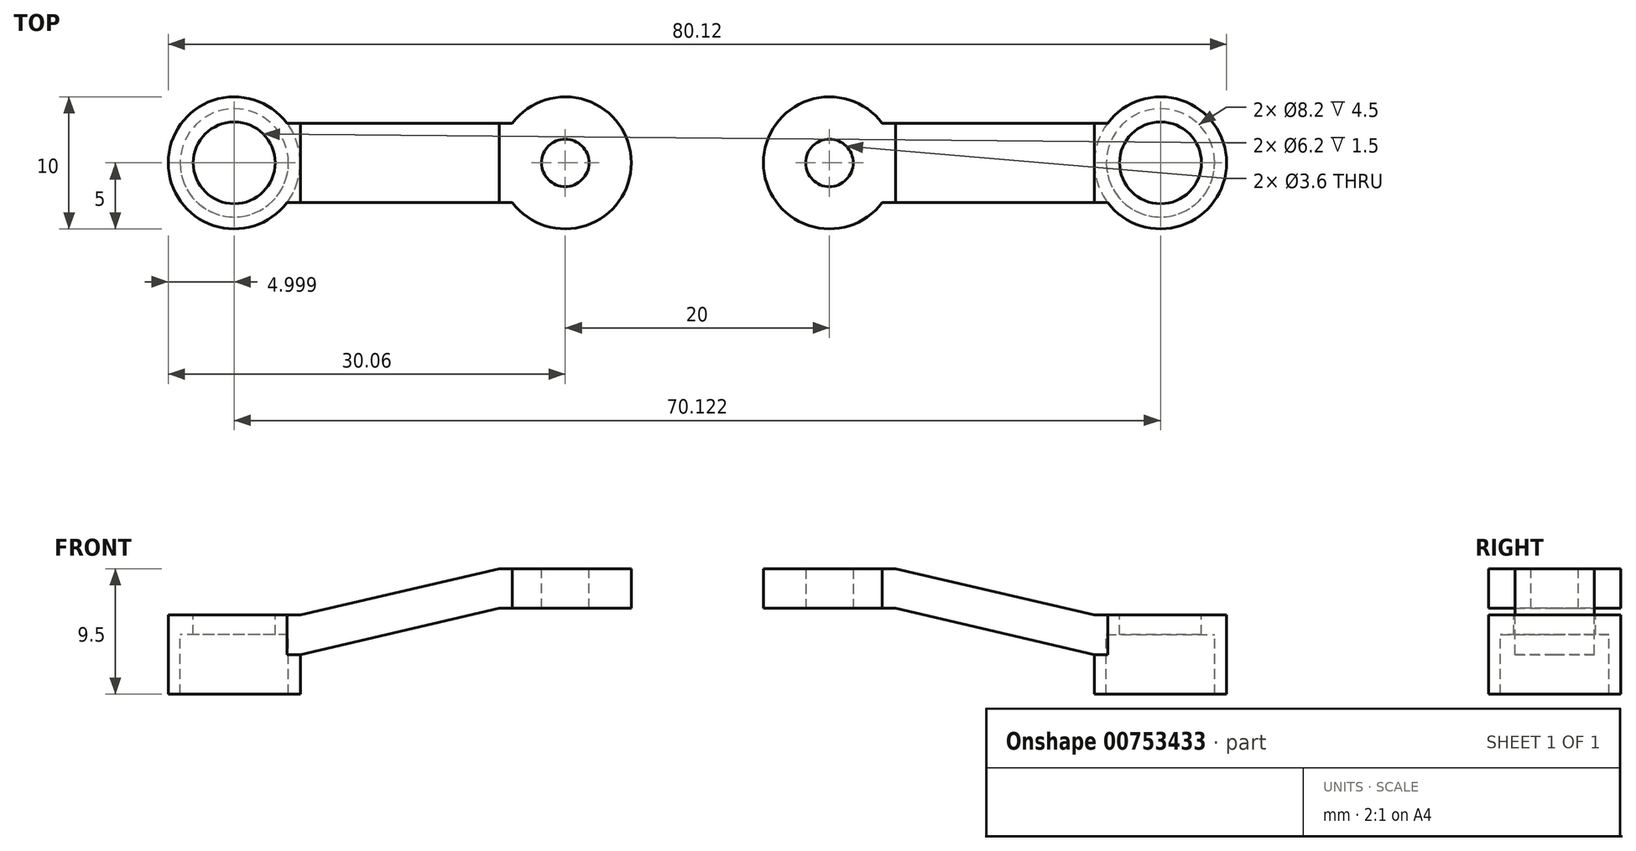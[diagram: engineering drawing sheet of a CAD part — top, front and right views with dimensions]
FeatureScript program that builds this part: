
annotation { "Feature Type Name" : "Feature", "Feature Type Description" : "" }
export const myFeature = defineFeature(function(context is Context, id is Id, definition is map)
    precondition{}
    {
        {
            var Q0;
            Q0=qCreatedBy(makeId("Front.planeOp"),FACE);
            var sketch = newSketch(context, id + "F0", { "sketchPlane" : qUnion([Q0])});
            skLineSegment(sketch, "E0", {"start": v(-30.06, 0) * mm, "end": v(-20.06, 0) * mm});
            skLineSegment(sketch, "E1", {"start": v(5, 3.5) * mm, "end": v(5, 6.5) * mm});
            skLineSegment(sketch, "E2", {"start": v(-20.06, 3) * mm, "end": v(-30.06, 3) * mm});
            skLineSegment(sketch, "E3", {"start": v(-30.06, 3) * mm, "end": v(-30.06, 0) * mm});
            skLineSegment(sketch, "E4", {"start": v(-5, 3.5) * mm, "end": v(-5, 6.5) * mm});
            skLineSegment(sketch, "E5", {"start": v(-20.06, 0) * mm, "end": v(-20.06, 3) * mm});
            skLineSegment(sketch, "E6", {"start": v(5, 6.5) * mm, "end": v(-5, 6.5) * mm});
            skLineSegment(sketch, "E7", {"start": v(5, 3.5) * mm, "end": v(-5, 3.5) * mm});
            skLineSegment(sketch, "E8", {"start": v(-20.06, 0) * mm, "end": v(-5, 3.5) * mm});
            skLineSegment(sketch, "E9", {"start": v(-5, 6.5) * mm, "end": v(-20.06, 3) * mm});
            skLineSegment(sketch, "E10", {"start": v(-25.06, 3) * mm, "end": v(-25.06, 0) * mm, "construction": true});
            skLineSegment(sketch, "E11", {"start": v(0, 6.5) * mm, "end": v(0, 3.5) * mm, "construction": true});
            skSolve(sketch);
        }
        {
            var Q0;
            Q0=makeQuery(id+"F0.imprint","IMPRINT",FACE,{"disambiguationData":[TD([[makeQuery(id+"F0.imprint","IMPRINT",EDGE,{"derivedFrom":sQuery(id+"F0.wireOp",EDGE,"E0")}),1.0]])]});
            var Q1;
            Q1=makeQuery(id+"F0.imprint","IMPRINT",FACE,{"disambiguationData":[TD([[makeQuery(id+"F0.imprint","IMPRINT",EDGE,{"derivedFrom":sQuery(id+"F0.wireOp",EDGE,"E4")}),1.0]])]});
            var Q2;
            Q2=makeQuery(id+"F0.imprint","IMPRINT",FACE,{"disambiguationData":[TD([[makeQuery(id+"F0.imprint","IMPRINT",EDGE,{"derivedFrom":sQuery(id+"F0.wireOp",EDGE,"E1")}),1.0]])]});
            extrude(context, id + "F1", {"entities" : qUnion([Q0, Q1, Q2]), "depth" : 7 * mm, "offsetDistance" : 25 * mm, "hasSecondDirection" : true, "secondDirectionOppositeDirection" : true, "secondDirectionDepth" : 7 * mm});
        }
        {
            var Q0;
            Q0=makeQuery(id+"F1.opExtrude","SWEPT_FACE",FACE,{"disambiguationData":[OSD([sQuery(id+"F0.wireOp",EDGE,"E6")])]});
            var sketch = newSketch(context, id + "F2", { "sketchPlane" : qUnion([Q0])});
            skCircle(sketch, "E12", {"center": v(0, 0) * mm, "radius": 4.1 * mm, "construction": true});
            skLineSegment(sketch, "E13.0", {"start": v(-20.06, 7) * mm, "end": v(-30.06, 7) * mm});
            skLineSegment(sketch, "E14.0", {"start": v(-30.06, -7) * mm, "end": v(-30.06, 7) * mm});
            skCircle(sketch, "E15", {"center": v(-25.06, 0) * mm, "radius": 4.1 * mm});
            skPoint(sketch, "E15.centerSnap0", {"position": v(-25.06, 7) * mm});
            skLineSegment(sketch, "E16.0", {"start": v(-5, 7) * mm, "end": v(-20.06, 7) * mm});
            skLineSegment(sketch, "E17.0", {"start": v(-20.06, -7) * mm, "end": v(-30.06, -7) * mm});
            skLineSegment(sketch, "E18.0", {"start": v(-5, -7) * mm, "end": v(-20.06, -7) * mm});
            skLineSegment(sketch, "E19.0", {"start": v(5, -7) * mm, "end": v(-5, -7) * mm});
            skLineSegment(sketch, "E20.0", {"start": v(5, -7) * mm, "end": v(5, 7) * mm});
            skLineSegment(sketch, "E21.0", {"start": v(5, 7) * mm, "end": v(-5, 7) * mm});
            skLineSegment(sketch, "E22", {"start": v(-21.06, 3) * mm, "end": v(-4, 3) * mm});
            skLineSegment(sketch, "E23", {"start": v(-21.06, -3) * mm, "end": v(-4, -3) * mm});
            skLineSegment(sketch, "E24", {"start": v(-25.06, 0) * mm, "end": v(0, 0) * mm, "construction": true});
            skLineSegment(sketch, "E25", {"start": v(-4, 3) * mm, "end": v(0, 3) * mm});
            skLineSegment(sketch, "E26", {"start": v(-4, -3) * mm, "end": v(0, -3) * mm});
            skCircle(sketch, "E27", {"center": v(-25.06, 0) * mm, "radius": 5 * mm});
            skArc(sketch, "E28", {"start": v(-4, -3) * mm, "mid": v(5, 0) * mm, "end": v(-4, 3) * mm});
            skArc(sketch, "E29", {"start": v(0, -3) * mm, "mid": v(2.12, 2.12) * mm, "end": v(-3, 0) * mm, "construction": true});
            skSolve(sketch);
        }
        {
            var Q0;
            {var subQ2=sQuery(id+"F2.wireOp",EDGE,"E13.0");Q0=makeQuery(id+"F2.imprint","IMPRINT",FACE,{"disambiguationData":[TD([[makeQuery(id+"F2.imprint","IMPRINT",EDGE,{"derivedFrom":subQ2}),1.0]])]});}
            var Q1;
            {var subQ5=sQuery(id+"F2.wireOp",EDGE,"E17.0");Q1=makeQuery(id+"F2.imprint","IMPRINT",FACE,{"disambiguationData":[TD([[makeQuery(id+"F2.imprint","IMPRINT",EDGE,{"derivedFrom":subQ5}),-1.0]])]});}
            var Q2;
            Q2=makeQuery(id+"F2.imprint","IMPRINT",FACE,{"disambiguationData":[TD([[makeQuery(id+"F2.imprint","IMPRINT",EDGE,{"derivedFrom":sQuery(id+"F2.wireOp",EDGE,"E15")}),1.0]])]});
            var Q3;
            {var subQ5=sQuery(id+"F2.wireOp",EDGE,"E21.0");Q3=makeQuery(id+"F2.imprint","IMPRINT",FACE,{"disambiguationData":[TD([[makeQuery(id+"F2.imprint","IMPRINT",EDGE,{"derivedFrom":subQ5}),1.0]])]});}
            var Q4;
            {var subQ7=sQuery(id+"F2.wireOp",EDGE,"E19.0");Q4=makeQuery(id+"F2.imprint","IMPRINT",FACE,{"disambiguationData":[TD([[makeQuery(id+"F2.imprint","IMPRINT",EDGE,{"derivedFrom":subQ7}),-1.0]])]});}
            var Q5;
            Q5=makeQuery(id+"F1.opExtrude","SWEPT_FACE",FACE,{"disambiguationData":[OSD([sQuery(id+"F0.wireOp",EDGE,"E0")])]});
            extrude(context, id + "F3", {"entities" : qUnion([Q0, Q1, Q2, Q3, Q4]), "operationType" : NewBodyOperationType.REMOVE, "endBound" : BoundingType.UP_TO_SURFACE, "oppositeDirection" : true, "depth" : 25 * mm, "endBoundEntityFace" : qUnion([Q5]), "offsetDistance" : 25 * mm});
        }
        {
            var Q0;
            Q0=qCreatedBy(makeId("Right.planeOp"),FACE);
            cPlane(context, id + "F4", {"entities" : qUnion([Q0]), "cplaneType" : CPlaneType.OFFSET, "offset" : 10 * mm, "width" : 150 * mm, "height" : 150 * mm});
        }
        {
            var Q0;
            Q0=makeQuery(id+"F1.opExtrude","SWEPT_FACE",FACE,{"disambiguationData":[OSD([sQuery(id+"F0.wireOp",EDGE,"E6")])]});
            var sketch = newSketch(context, id + "F5", { "sketchPlane" : qUnion([Q0])});
            skCircle(sketch, "E30", {"center": v(0, 0) * mm, "radius": 1.5 * mm});
            skLineSegment(sketch, "E31", {"start": v(0, 0) * mm, "end": v(1.5, 0) * mm, "construction": true});
            skSolve(sketch);
        }
        {
            var Q0;
            Q0=makeQuery(id+"F1.opExtrude","SWEPT_BODY",BODY,{"disambiguationData":[OSD([sQuery(id+"F0.wireOp",EDGE,"E0"),sQuery(id+"F0.wireOp",EDGE,"E1"),sQuery(id+"F0.wireOp",EDGE,"E2"),sQuery(id+"F0.wireOp",EDGE,"E3"),sQuery(id+"F0.wireOp",EDGE,"E6"),sQuery(id+"F0.wireOp",EDGE,"E7"),sQuery(id+"F0.wireOp",EDGE,"E8"),sQuery(id+"F0.wireOp",EDGE,"E9")])]});
            var Q1;
            Q1=qCreatedBy(id+"F4.planeOp",FACE);
            mirror(context, id + "F6", {"entities" : qUnion([Q0]), "mirrorPlane" : qUnion([Q1])});
        }
        {
            var Q0;
            Q0=makeQuery(id+"F5.imprint","IMPRINT",FACE,{"disambiguationData":[TD([[makeQuery(id+"F5.imprint","IMPRINT",EDGE,{"derivedFrom":sQuery(id+"F5.wireOp",EDGE,"E30")}),1.0]])]});
            extrude(context, id + "F7", {"entities" : qUnion([Q0]), "operationType" : NewBodyOperationType.ADD, "depth" : 8 * mm, "offsetDistance" : 25 * mm});
        }
        {
            var Q0;
            Q0=makeQuery(id+"F6.opPattern","COPY",FACE,{"derivedFrom":makeQuery(id+"F1.opExtrude","SWEPT_FACE",FACE,{"disambiguationData":[OSD([sQuery(id+"F0.wireOp",EDGE,"E7")])]}),"instanceName":"1"});
            var sketch = newSketch(context, id + "F8", { "sketchPlane" : qUnion([Q0])});
            skCircle(sketch, "E32", {"center": v(20, 0) * mm, "radius": 1.5 * mm});
            skLineSegment(sketch, "E33", {"start": v(20, 0) * mm, "end": v(18.5, 0) * mm, "construction": true});
            skArc(sketch, "E34.0", {"start": v(24, -3) * mm, "mid": v(15, 0) * mm, "end": v(24, 3) * mm});
            skSolve(sketch);
        }
        {
            var Q0;
            Q0=makeQuery(id+"F8.imprint","IMPRINT",FACE,{"disambiguationData":[TD([[makeQuery(id+"F8.imprint","IMPRINT",EDGE,{"derivedFrom":sQuery(id+"F8.wireOp",EDGE,"E32")}),1.0]])]});
            extrude(context, id + "F9", {"entities" : qUnion([Q0]), "operationType" : NewBodyOperationType.ADD, "depth" : 8 * mm, "offsetDistance" : 25 * mm});
        }
        {
            var Q0;
            Q0=makeQuery(id+"F1.opExtrude","SWEPT_FACE",FACE,{"disambiguationData":[OSD([sQuery(id+"F0.wireOp",EDGE,"E6")])]});
            var sketch = newSketch(context, id + "F10", { "sketchPlane" : qUnion([Q0])});
            skCircle(sketch, "E35.0", {"center": v(0, 0) * mm, "radius": 1.5 * mm});
            skCircle(sketch, "E36", {"center": v(0, 0) * mm, "radius": 2.5 * mm});
            skSolve(sketch);
        }
        {
            var Q0;
            Q0=makeQuery(id+"F10.imprint","IMPRINT",FACE,{"disambiguationData":[TD([[makeQuery(id+"F10.imprint","IMPRINT",EDGE,{"derivedFrom":sQuery(id+"F10.wireOp",EDGE,"E35.0")}),-1.0]])]});
            extrude(context, id + "F11", {"entities" : qUnion([Q0]), "operationType" : NewBodyOperationType.ADD, "depth" : 2 * mm, "offsetDistance" : 25 * mm});
        }
        {
            var Q0;
            Q0=makeQuery(id+"F6.opPattern","COPY",FACE,{"derivedFrom":makeQuery(id+"F1.opExtrude","SWEPT_FACE",FACE,{"disambiguationData":[OSD([sQuery(id+"F0.wireOp",EDGE,"E7")])]}),"instanceName":"1"});
            var sketch = newSketch(context, id + "F12", { "sketchPlane" : qUnion([Q0])});
            skCircle(sketch, "E37.0", {"center": v(20, 0) * mm, "radius": 1.5 * mm});
            skCircle(sketch, "E38", {"center": v(20, 0) * mm, "radius": 2.5 * mm});
            skSolve(sketch);
        }
        {
            var Q0;
            Q0=makeQuery(id+"F12.imprint","IMPRINT",FACE,{"disambiguationData":[TD([[makeQuery(id+"F12.imprint","IMPRINT",EDGE,{"derivedFrom":sQuery(id+"F12.wireOp",EDGE,"E37.0")}),-1.0]])]});
            extrude(context, id + "F13", {"entities" : qUnion([Q0]), "operationType" : NewBodyOperationType.ADD, "depth" : 2 * mm, "offsetDistance" : 25 * mm});
        }
        {
            var Q0;
            Q0=makeQuery(id+"F1.opExtrude","SWEPT_FACE",FACE,{"disambiguationData":[OSD([sQuery(id+"F0.wireOp",EDGE,"E0")])]});
            var sketch = newSketch(context, id + "F14", { "sketchPlane" : qUnion([Q0])});
            skArc(sketch, "E39.0", {"start": v(-21.33, 3.33) * mm, "mid": v(-30.06, 0) * mm, "end": v(-21.33, -3.33) * mm});
            skCircle(sketch, "E40", {"center": v(-25.06, 0) * mm, "radius": 7 * mm});
            skCircle(sketch, "E41.0", {"center": v(-25.06, 0) * mm, "radius": 4.1 * mm});
            skCircle(sketch, "E42", {"center": v(-25.06, 0) * mm, "radius": 5 * mm});
            skSolve(sketch);
        }
        {
            var Q0;
            Q0=makeQuery(id+"F14.imprint","IMPRINT",FACE,{"disambiguationData":[TD([[makeQuery(id+"F14.imprint","IMPRINT",EDGE,{"derivedFrom":sQuery(id+"F14.wireOp",EDGE,"E41.0")}),-1.0]])]});
            extrude(context, id + "F15", {"entities" : qUnion([Q0]), "operationType" : NewBodyOperationType.ADD, "depth" : 3 * mm, "offsetDistance" : 25 * mm});
        }
        {
            var Q0;
            Q0=makeQuery(id+"F1.opExtrude","SWEPT_FACE",FACE,{"disambiguationData":[OSD([sQuery(id+"F0.wireOp",EDGE,"E2")])]});
            var sketch = newSketch(context, id + "F16", { "sketchPlane" : qUnion([Q0])});
            skCircle(sketch, "E43.0", {"center": v(-25.06, 0) * mm, "radius": 4.1 * mm});
            skCircle(sketch, "E44", {"center": v(-25.06, 0) * mm, "radius": 3.1 * mm});
            skSolve(sketch);
        }
        {
            var Q0;
            Q0=makeQuery(id+"F16.imprint","IMPRINT",FACE,{"disambiguationData":[TD([[makeQuery(id+"F16.imprint","IMPRINT",EDGE,{"derivedFrom":sQuery(id+"F16.wireOp",EDGE,"E43.0")}),-1.0]])]});
            extrude(context, id + "F17", {"entities" : qUnion([Q0]), "operationType" : NewBodyOperationType.ADD, "oppositeDirection" : true, "depth" : 1.5 * mm, "offsetDistance" : 25 * mm});
        }
        {
            var Q0;
            Q0=makeQuery(id+"F15.opExtrude","CAP_FACE",FACE,{"disambiguationData":[OSD([sQuery(id+"F14.wireOp",EDGE,"E40"),sQuery(id+"F14.wireOp",EDGE,"E41.0")])],"isStart":false});
            var sketch = newSketch(context, id + "F18", { "sketchPlane" : qUnion([Q0])});
            skCircle(sketch, "E45.0", {"center": v(-25.06, 0) * mm, "radius": 3.1 * mm});
            skCircle(sketch, "E46.0", {"center": v(-25.06, 0) * mm, "radius": 4.1 * mm});
            skSolve(sketch);
        }
        {
            var Q0;
            Q0=makeQuery(id+"F18.imprint","IMPRINT",FACE,{"disambiguationData":[TD([[makeQuery(id+"F18.imprint","IMPRINT",EDGE,{"derivedFrom":sQuery(id+"F18.wireOp",EDGE,"E45.0")}),-1.0]])]});
            extrude(context, id + "F19", {"entities" : qUnion([Q0]), "operationType" : NewBodyOperationType.ADD, "oppositeDirection" : true, "depth" : 1.5 * mm, "offsetDistance" : 25 * mm});
        }
        {
            var Q0;
            Q0=makeQuery(id+"F6.opPattern","COPY",FACE,{"derivedFrom":makeQuery(id+"F1.opExtrude","SWEPT_FACE",FACE,{"disambiguationData":[OSD([sQuery(id+"F0.wireOp",EDGE,"E0")])]}),"instanceName":"1"});
            var sketch = newSketch(context, id + "F20", { "sketchPlane" : qUnion([Q0])});
            skArc(sketch, "E47.0", {"start": v(41.06, 3) * mm, "mid": v(50.06, 0) * mm, "end": v(41.06, -3) * mm});
            skCircle(sketch, "E48.0", {"center": v(45.06, 0) * mm, "radius": 4.1 * mm});
            skCircle(sketch, "E49", {"center": v(45.06, 0) * mm, "radius": 5 * mm});
            skSolve(sketch);
        }
        {
            var Q0;
            Q0 = qSketchRegion(id + "F20", true);
            var Q1;
            Q1=makeQuery(id+"F20.imprint","IMPRINT",FACE,{"disambiguationData":[TD([[makeQuery(id+"F20.imprint","IMPRINT",EDGE,{"derivedFrom":sQuery(id+"F20.wireOp",EDGE,"E48.0")}),1.0]])]});
            extrude(context, id + "F21", {"entities" : qUnion([Q0, Q1]), "operationType" : NewBodyOperationType.ADD, "depth" : 3 * mm, "offsetDistance" : 25 * mm});
        }
        {
            var Q0;
            Q0=makeQuery(id+"F21.opExtrude","CAP_FACE",FACE,{"disambiguationData":[OSD([sQuery(id+"F20.wireOp",EDGE,"E48.0"),sQuery(id+"F20.wireOp",EDGE,"E49")])],"isStart":false});
            var sketch = newSketch(context, id + "F22", { "sketchPlane" : qUnion([Q0])});
            skCircle(sketch, "E50", {"center": v(45.06, 0) * mm, "radius": 3.1 * mm});
            skCircle(sketch, "E51.0", {"center": v(45.06, 0) * mm, "radius": 4.1 * mm});
            skSolve(sketch);
        }
        {
            var Q0;
            Q0=makeQuery(id+"F22.imprint","IMPRINT",FACE,{"disambiguationData":[TD([[makeQuery(id+"F22.imprint","IMPRINT",EDGE,{"derivedFrom":sQuery(id+"F22.wireOp",EDGE,"E50")}),-1.0]])]});
            extrude(context, id + "F23", {"entities" : qUnion([Q0]), "operationType" : NewBodyOperationType.ADD, "oppositeDirection" : true, "depth" : 1.5 * mm, "offsetDistance" : 25 * mm});
        }
        {
            var Q0;
            Q0=makeQuery(id+"F6.opPattern","COPY",FACE,{"derivedFrom":makeQuery(id+"F1.opExtrude","SWEPT_FACE",FACE,{"disambiguationData":[OSD([sQuery(id+"F0.wireOp",EDGE,"E2")])]}),"instanceName":"1"});
            var sketch = newSketch(context, id + "F24", { "sketchPlane" : qUnion([Q0])});
            skCircle(sketch, "E52.0", {"center": v(45.06, 0) * mm, "radius": 4.1 * mm});
            skCircle(sketch, "E53.0", {"center": v(45.06, 0) * mm, "radius": 3.1 * mm});
            skSolve(sketch);
        }
        {
            var Q0;
            Q0=makeQuery(id+"F24.imprint","IMPRINT",FACE,{"disambiguationData":[TD([[makeQuery(id+"F24.imprint","IMPRINT",EDGE,{"derivedFrom":sQuery(id+"F24.wireOp",EDGE,"E52.0")}),1.0]])]});
            extrude(context, id + "F25", {"entities" : qUnion([Q0]), "operationType" : NewBodyOperationType.ADD, "oppositeDirection" : true, "depth" : 1.5 * mm, "offsetDistance" : 25 * mm});
        }
        {
            var Q0;
            Q0=makeQuery(id+"F7.opExtrude","CAP_FACE",FACE,{"disambiguationData":[OSD([sQuery(id+"F5.wireOp",EDGE,"E30")])],"isStart":false});
            var sketch = newSketch(context, id + "F26", { "sketchPlane" : qUnion([Q0])});
            skCircle(sketch, "E54.0", {"center": v(0, 0) * mm, "radius": 1.5 * mm, "construction": true});
            skCircle(sketch, "E55", {"center": v(0, 0) * mm, "radius": 1.8 * mm});
            skSolve(sketch);
        }
        {
            var Q0;
            Q0=makeQuery(id+"F26.imprint","IMPRINT",FACE,{"disambiguationData":[TD([[makeQuery(id+"F26.imprint","IMPRINT",EDGE,{"derivedFrom":sQuery(id+"F26.wireOp",EDGE,"E55")}),1.0]])]});
            var Q1;
            Q1=makeQuery(id+"F26.imprint","IMPRINT",FACE,{"disambiguationData":[TD([[makeQuery(id+"F26.imprint","IMPRINT",EDGE,{"derivedFrom":makeQuery(id+"F7.opExtrude","CAP_EDGE",EDGE,{"disambiguationData":[OSD([sQuery(id+"F5.wireOp",EDGE,"E30")])],"isStart":false})}),1.0]])]});
            var Q2;
            Q2=makeQuery(id+"F1.opExtrude","SWEPT_FACE",FACE,{"disambiguationData":[OSD([sQuery(id+"F0.wireOp",EDGE,"E7")])]});
            extrude(context, id + "F27", {"entities" : qUnion([Q0, Q1]), "operationType" : NewBodyOperationType.REMOVE, "endBound" : BoundingType.UP_TO_SURFACE, "oppositeDirection" : true, "depth" : 25 * mm, "endBoundEntityFace" : qUnion([Q2]), "offsetDistance" : 25 * mm});
        }
        {
            var Q0;
            Q0=makeQuery(id+"F9.opExtrude","CAP_FACE",FACE,{"disambiguationData":[OSD([sQuery(id+"F8.wireOp",EDGE,"E32")])],"isStart":false});
            var sketch = newSketch(context, id + "F28", { "sketchPlane" : qUnion([Q0])});
            skCircle(sketch, "E56", {"center": v(20, 0) * mm, "radius": 1.8 * mm});
            skSolve(sketch);
        }
        {
            var Q0;
            Q0=makeQuery(id+"F28.imprint","IMPRINT",FACE,{"disambiguationData":[TD([[makeQuery(id+"F28.imprint","IMPRINT",EDGE,{"derivedFrom":sQuery(id+"F28.wireOp",EDGE,"E56")}),1.0]])]});
            var Q1;
            Q1=makeQuery(id+"F28.imprint","IMPRINT",FACE,{"disambiguationData":[TD([[makeQuery(id+"F28.imprint","IMPRINT",EDGE,{"derivedFrom":makeQuery(id+"F9.opExtrude","CAP_EDGE",EDGE,{"disambiguationData":[OSD([sQuery(id+"F8.wireOp",EDGE,"E32")])],"isStart":false})}),1.0]])]});
            var Q2;
            Q2=makeQuery(id+"F6.opPattern","COPY",FACE,{"derivedFrom":makeQuery(id+"F1.opExtrude","SWEPT_FACE",FACE,{"disambiguationData":[OSD([sQuery(id+"F0.wireOp",EDGE,"E6")])]}),"instanceName":"1"});
            extrude(context, id + "F29", {"entities" : qUnion([Q0, Q1]), "operationType" : NewBodyOperationType.REMOVE, "endBound" : BoundingType.UP_TO_SURFACE, "oppositeDirection" : true, "depth" : 25 * mm, "endBoundEntityFace" : qUnion([Q2]), "offsetDistance" : 25 * mm});
        }
        {
            var Q0;
            Q0=makeQuery(id+"F11.opExtrude","CAP_FACE",FACE,{"disambiguationData":[OSD([sQuery(id+"F10.wireOp",EDGE,"E35.0"),sQuery(id+"F10.wireOp",EDGE,"E36")])],"isStart":false});
            var sketch = newSketch(context, id + "F30", { "sketchPlane" : qUnion([Q0])});
            skSolve(sketch);
        }
        {
            var Q0;
            Q0 = qSketchRegion(id + "F30", true);
            var Q1;
            {var subQ0=sQuery(id+"F10.wireOp",EDGE,"E36");Q1=makeQuery(id+"F30.imprint","IMPRINT",FACE,{"disambiguationData":[TD([[makeQuery(id+"F30.imprint","IMPRINT",EDGE,{"derivedFrom":makeQuery(id+"F11.opExtrude","CAP_EDGE",EDGE,{"disambiguationData":[OSD([subQ0])],"isStart":false})}),1.0]])]});}
            var Q2;
            Q2=makeQuery(id+"F1.opExtrude","SWEPT_FACE",FACE,{"disambiguationData":[OSD([sQuery(id+"F0.wireOp",EDGE,"E6")])]});
            extrude(context, id + "F31", {"entities" : qUnion([Q0, Q1]), "operationType" : NewBodyOperationType.REMOVE, "endBound" : BoundingType.UP_TO_SURFACE, "oppositeDirection" : true, "depth" : 25 * mm, "endBoundEntityFace" : qUnion([Q2]), "offsetDistance" : 25 * mm});
        }
        {
            var Q0;
            Q0=makeQuery(id+"F13.opExtrude","CAP_FACE",FACE,{"disambiguationData":[OSD([sQuery(id+"F12.wireOp",EDGE,"E37.0"),sQuery(id+"F12.wireOp",EDGE,"E38")])],"isStart":false});
            var sketch = newSketch(context, id + "F32", { "sketchPlane" : qUnion([Q0])});
            skSolve(sketch);
        }
        {
            var Q0;
            Q0 = qSketchRegion(id + "F32", true);
            var Q1;
            {var subQ0=sQuery(id+"F12.wireOp",EDGE,"E38");Q1=makeQuery(id+"F32.imprint","IMPRINT",FACE,{"disambiguationData":[TD([[makeQuery(id+"F32.imprint","IMPRINT",EDGE,{"derivedFrom":makeQuery(id+"F13.opExtrude","CAP_EDGE",EDGE,{"disambiguationData":[OSD([subQ0])],"isStart":false})}),1.0]])]});}
            var Q2;
            Q2=makeQuery(id+"F6.opPattern","COPY",FACE,{"derivedFrom":makeQuery(id+"F1.opExtrude","SWEPT_FACE",FACE,{"disambiguationData":[OSD([sQuery(id+"F0.wireOp",EDGE,"E7")])]}),"instanceName":"1"});
            extrude(context, id + "F33", {"entities" : qUnion([Q0, Q1]), "operationType" : NewBodyOperationType.REMOVE, "endBound" : BoundingType.UP_TO_SURFACE, "oppositeDirection" : true, "depth" : 25 * mm, "endBoundEntityFace" : qUnion([Q2]), "offsetDistance" : 25 * mm});
        }
        {
            var Q0;
            Q0=makeQuery(id+"F19.boolean.opBoolean","MERGE",FACE,{"derivedFrom":[makeQuery(id+"F15.opExtrude","CAP_FACE",FACE,{"disambiguationData":[OSD([sQuery(id+"F14.wireOp",EDGE,"E41.0"),sQuery(id+"F14.wireOp",EDGE,"E42")])],"isStart":false}),makeQuery(id+"F19.opExtrude","CAP_FACE",FACE,{"disambiguationData":[OSD([sQuery(id+"F18.wireOp",EDGE,"E45.0"),sQuery(id+"F18.wireOp",EDGE,"E46.0")])],"isStart":true})]});
            var sketch = newSketch(context, id + "F34", { "sketchPlane" : qUnion([Q0])});
            skCircle(sketch, "E57.0", {"center": v(-25.06, 0) * mm, "radius": 3.1 * mm});
            skCircle(sketch, "E58.0", {"center": v(-25.06, 0) * mm, "radius": 4.1 * mm});
            skSolve(sketch);
        }
        {
            var Q0;
            Q0=makeQuery(id+"F34.imprint","IMPRINT",FACE,{"disambiguationData":[TD([[makeQuery(id+"F34.imprint","IMPRINT",EDGE,{"derivedFrom":sQuery(id+"F34.wireOp",EDGE,"E57.0")}),-1.0]])]});
            extrude(context, id + "F35", {"entities" : qUnion([Q0]), "operationType" : NewBodyOperationType.REMOVE, "endBound" : BoundingType.UP_TO_NEXT, "oppositeDirection" : true, "depth" : 25 * mm, "offsetDistance" : 25 * mm});
        }
        {
            var Q0;
            Q0=makeQuery(id+"F23.boolean.opBoolean","MERGE",FACE,{"derivedFrom":[makeQuery(id+"F21.opExtrude","CAP_FACE",FACE,{"disambiguationData":[OSD([sQuery(id+"F20.wireOp",EDGE,"E48.0"),sQuery(id+"F20.wireOp",EDGE,"E49")])],"isStart":false}),makeQuery(id+"F23.opExtrude","CAP_FACE",FACE,{"disambiguationData":[OSD([sQuery(id+"F22.wireOp",EDGE,"E50"),sQuery(id+"F22.wireOp",EDGE,"E51.0")])],"isStart":true})]});
            var sketch = newSketch(context, id + "F36", { "sketchPlane" : qUnion([Q0])});
            skCircle(sketch, "E59.0", {"center": v(45.06, 0) * mm, "radius": 4.1 * mm});
            skCircle(sketch, "E60.0", {"center": v(45.06, 0) * mm, "radius": 3.1 * mm});
            skSolve(sketch);
        }
        {
            var Q0;
            Q0 = qSketchRegion(id + "F36", true);
            extrude(context, id + "F37", {"entities" : qUnion([Q0]), "operationType" : NewBodyOperationType.REMOVE, "endBound" : BoundingType.UP_TO_NEXT, "oppositeDirection" : true, "depth" : 25 * mm, "offsetDistance" : 25 * mm});
        }
    });
